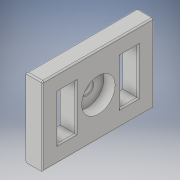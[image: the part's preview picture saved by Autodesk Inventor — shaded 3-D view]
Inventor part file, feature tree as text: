
AUTODESK INVENTOR PART (.ipt)
format: ipt  version: 2017 (Build 210142000, 142)  size: 174,592 bytes
history: native  units: in
note: dims shown in document units (in); Inventor stores cm internally (conversion verified against a paired STEP export)
features: sketch x3, extrude x3, projected_geometry x2, hole x1, fillet x1
ambient origin geometry x8: Origin, YZ Plane, XZ Plane, XY Plane, X Axis, Y Axis, Z Axis, Center Point
bodies: Solid1 (feature_tree)
feature tree (10):
  sketch  "Sketch1"  dims[d8=0.51in d9=0.1975in]
  extrude  "Extrusion1"  Depth=0.1975in
  extrude  "Extrusion2"  Depth=0.1825in
  extrude  "Extrusion5"  Depth=0.375in
  hole  "Hole1"  [1 undecoded]
  fillet  "Fillet1"  Radius=0.125in
  sketch  "Sketch2"  dims[d10=0.1775in d11=0.1825in]
  projected_geometry  "Projected Loop1"
  sketch  "Sketch5"  dims[d12=0.1875in d13=0.0in d14=0.375in d15=0.4375in d17=0.125in d18=0.0in d28=0.1825in d31=0.247in d32=0.1235in d37=1.25in d38=1.25in d39=0.875in d43=0.1975in d48=0.51in d49=0.1825in d50=1.0in d51=0.0in d52=1.25in d53=0.625in d54=0.145in d55=0.38in d56=0.375in d57=0.25in d58=0.5635in d59=0.588in d60=0.8108in d61=0.015in]
  projected_geometry  "Projected Loop6"
note: 1 required parameter value undecoded (feature->parameter linkage not recoverable at this tier; creation-order binding heuristic only, values carry confidence <= 0.55)
